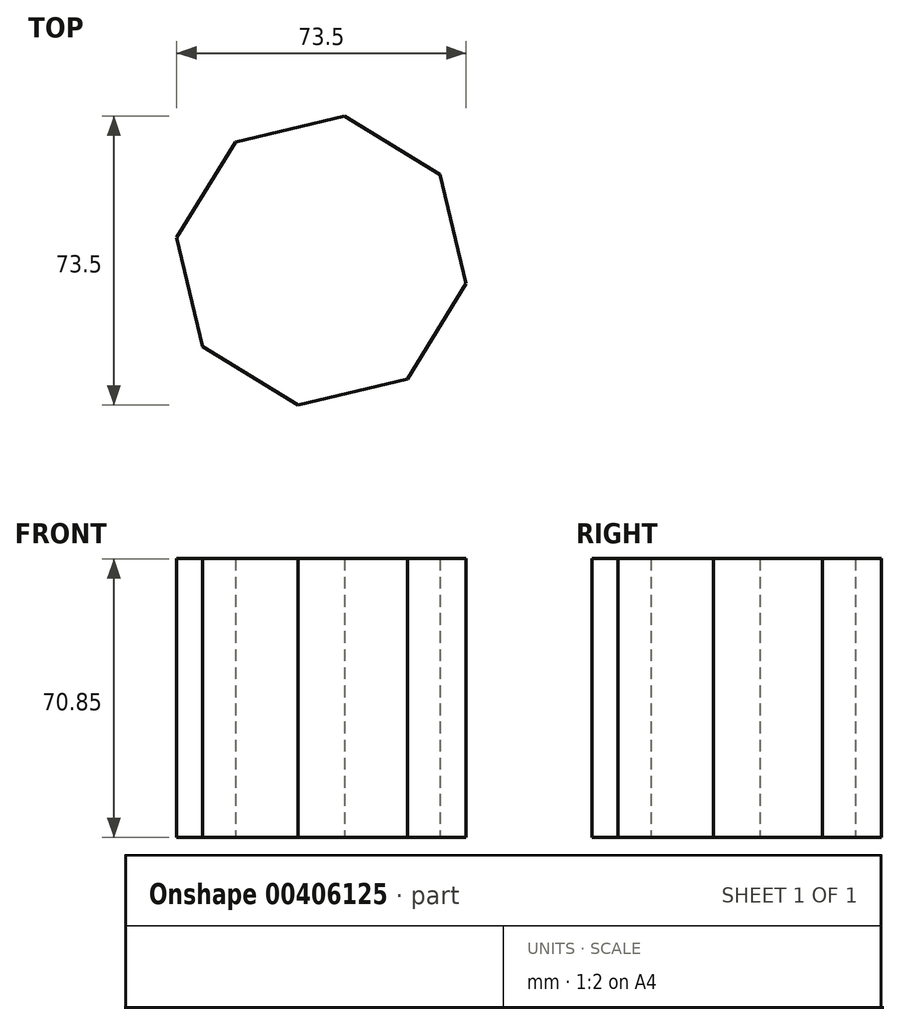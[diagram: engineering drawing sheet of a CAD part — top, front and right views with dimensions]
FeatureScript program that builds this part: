
annotation { "Feature Type Name" : "Feature", "Feature Type Description" : "" }
export const myFeature = defineFeature(function(context is Context, id is Id, definition is map)
    precondition{}
    {
        {
            var Q0;
            Q0=qCreatedBy(makeId("Top.planeOp"),FACE);
            var sketch = newSketch(context, id + "F0", { "sketchPlane" : qUnion([Q0])});
            skCircle(sketch, "E0.cCircle", {"center": v(-43.57, 33.45) * mm, "radius": 34.39 * mm, "construction": true});
            skLineSegment(sketch, "E0.0", {"start": v(-21.75, 3.3) * mm, "end": v(-49.46, -3.3) * mm});
            skLineSegment(sketch, "E0.1", {"start": v(-49.46, -3.3) * mm, "end": v(-73.72, 11.63) * mm});
            skLineSegment(sketch, "E0.2", {"start": v(-73.72, 11.63) * mm, "end": v(-80.32, 39.34) * mm});
            skLineSegment(sketch, "E0.3", {"start": v(-80.32, 39.34) * mm, "end": v(-65.39, 63.6) * mm});
            skLineSegment(sketch, "E0.4", {"start": v(-65.39, 63.6) * mm, "end": v(-37.68, 70.2) * mm});
            skLineSegment(sketch, "E0.5", {"start": v(-37.68, 70.2) * mm, "end": v(-13.42, 55.27) * mm});
            skLineSegment(sketch, "E0.6", {"start": v(-13.42, 55.27) * mm, "end": v(-6.82, 27.56) * mm});
            skLineSegment(sketch, "E0.7", {"start": v(-6.82, 27.56) * mm, "end": v(-21.75, 3.3) * mm});
            skPoint(sketch, "E0.0.midPoint", {"position": v(-35.6, 0) * mm});
            skSolve(sketch);
        }
        {
            var Q0;
            Q0=makeQuery(id+"F0.imprint","IMPRINT",FACE,{"disambiguationData":[TD([[makeQuery(id+"F0.imprint","IMPRINT",EDGE,{"derivedFrom":sQuery(id+"F0.wireOp",EDGE,"E0.0")}),-1.0]])]});
            extrude(context, id + "F1", {"entities" : qUnion([Q0]), "depth" : 70.85 * mm});
        }
    });
